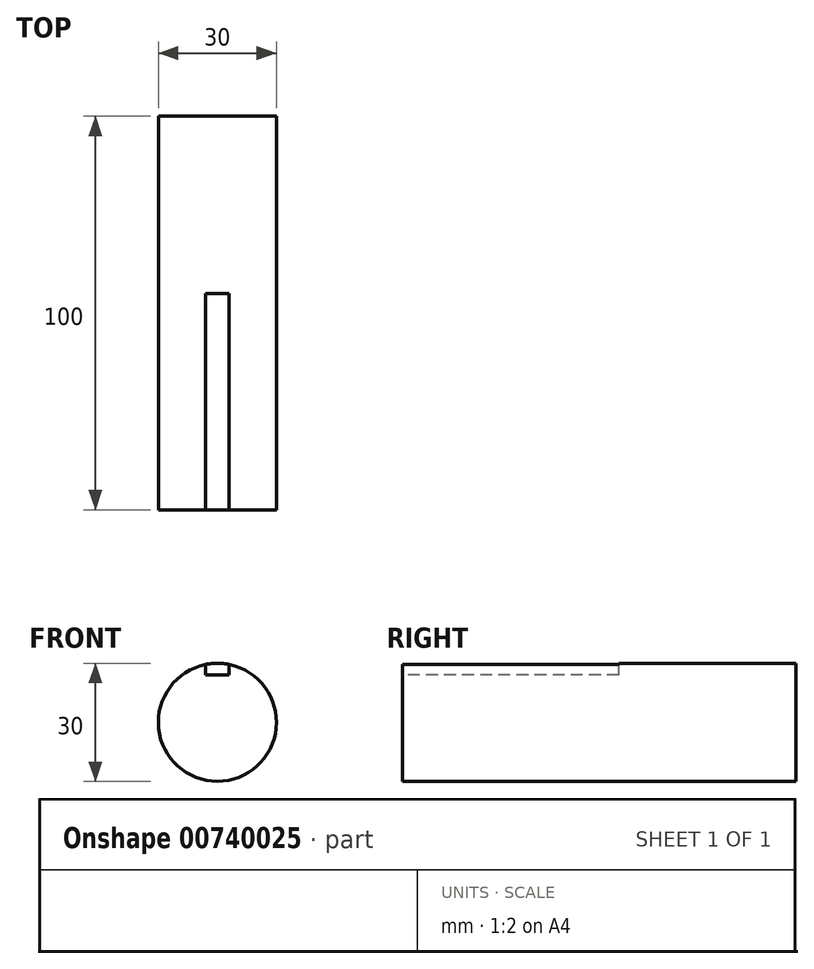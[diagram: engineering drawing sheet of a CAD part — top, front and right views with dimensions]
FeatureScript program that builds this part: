
annotation { "Feature Type Name" : "Feature", "Feature Type Description" : "" }
export const myFeature = defineFeature(function(context is Context, id is Id, definition is map)
    precondition{}
    {
        {
            var Q0;
            Q0=qCreatedBy(makeId("Front.planeOp"),FACE);
            var sketch = newSketch(context, id + "F0", { "sketchPlane" : qUnion([Q0])});
            skCircle(sketch, "E0", {"center": v(0, 0) * mm, "radius": 15 * mm});
            skSolve(sketch);
        }
        {
            var Q0;
            Q0=makeQuery(id+"F0.imprint","IMPRINT",FACE,{"disambiguationData":[TD([[makeQuery(id+"F0.imprint","IMPRINT",EDGE,{"derivedFrom":sQuery(id+"F0.wireOp",EDGE,"E0")}),1.0]])]});
            extrude(context, id + "F1", {"entities" : qUnion([Q0]), "oppositeDirection" : true, "depth" : 100 * mm, "offsetDistance" : 25 * mm});
        }
        {
            var Q0;
            Q0=makeQuery(id+"F1.opExtrude","CAP_FACE",FACE,{"disambiguationData":[OSD([sQuery(id+"F0.wireOp",EDGE,"E0")])],"isStart":true});
            var sketch = newSketch(context, id + "F2", { "sketchPlane" : qUnion([Q0])});
            skArc(sketch, "E1", {"start": v(3, 14.7) * mm, "mid": v(0, 15) * mm, "end": v(-3, 14.7) * mm});
            skLineSegment(sketch, "E2", {"start": v(-3, 12) * mm, "end": v(-3, 14.7) * mm});
            skLineSegment(sketch, "E3", {"start": v(3, 14.7) * mm, "end": v(3, 12) * mm});
            skLineSegment(sketch, "E4", {"start": v(-3, 12) * mm, "end": v(3, 12) * mm});
            skSolve(sketch);
        }
        {
            var Q0;
            Q0=makeQuery(id+"F2.imprint","IMPRINT",FACE,{"disambiguationData":[TD([[makeQuery(id+"F2.imprint","IMPRINT",EDGE,{"derivedFrom":sQuery(id+"F2.wireOp",EDGE,"E1")}),1.0]])]});
            extrude(context, id + "F3", {"entities" : qUnion([Q0]), "operationType" : NewBodyOperationType.REMOVE, "oppositeDirection" : true, "depth" : 55 * mm, "offsetDistance" : 25 * mm});
        }
    });
